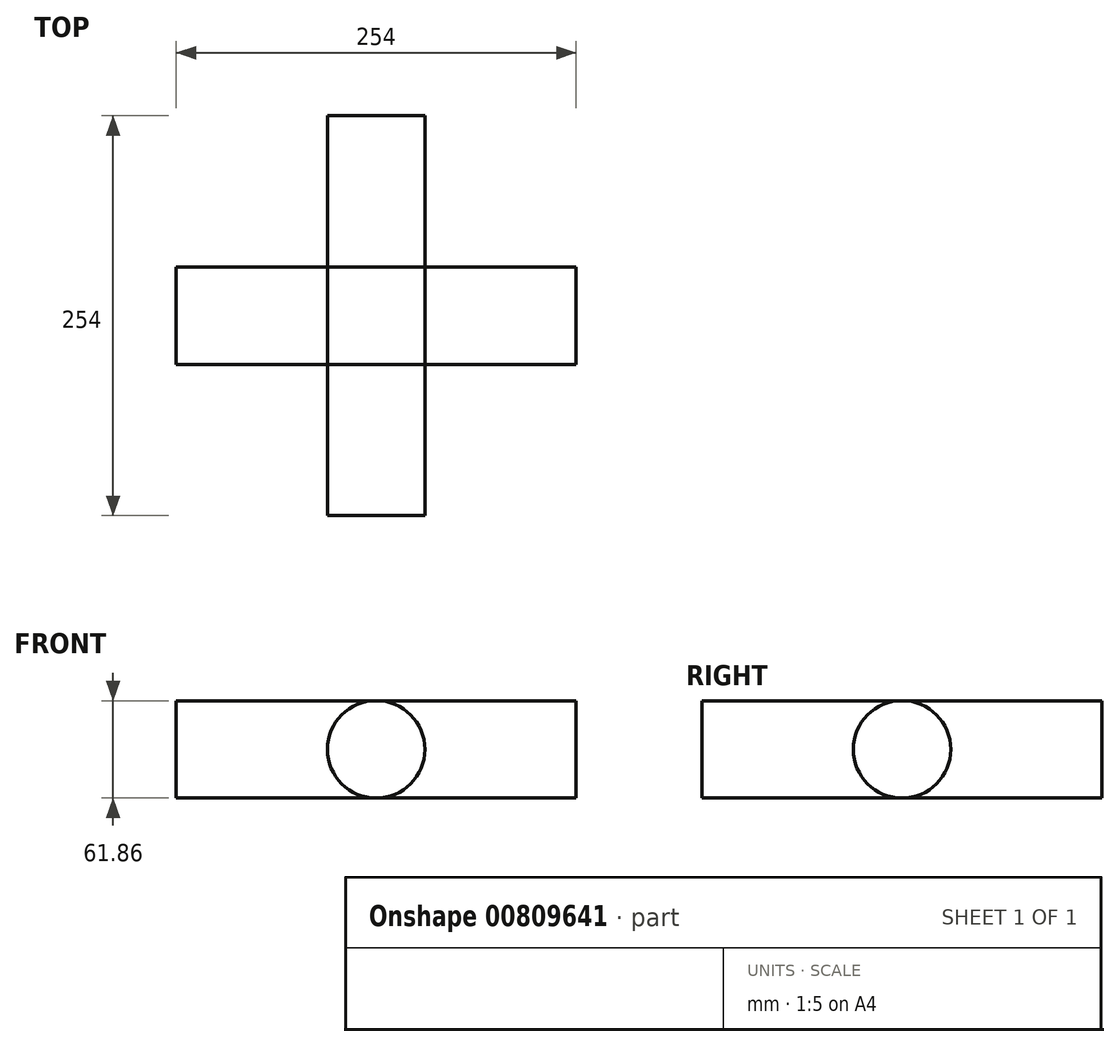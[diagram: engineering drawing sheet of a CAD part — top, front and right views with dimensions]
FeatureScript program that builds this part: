
annotation { "Feature Type Name" : "Feature", "Feature Type Description" : "" }
export const myFeature = defineFeature(function(context is Context, id is Id, definition is map)
    precondition{}
    {
        {
            var Q0;
            Q0=qCreatedBy(makeId("Front.planeOp"),FACE);
            var sketch = newSketch(context, id + "F0", { "sketchPlane" : qUnion([Q0])});
            skCircle(sketch, "E0", {"center": v(0, 0) * mm, "radius": 30.93 * mm});
            skSolve(sketch);
        }
        {
            var Q0;
            Q0 = qSketchRegion(id + "F0", true);
            extrude(context, id + "F1", {"entities" : qUnion([Q0]), "endBound" : BoundingType.SYMMETRIC, "depth" : 254 * mm, "offsetDistance" : 25.4 * mm});
        }
        {
            var Q0;
            Q0=qCreatedBy(makeId("Front.planeOp"),FACE);
            var sketch = newSketch(context, id + "F2", { "sketchPlane" : qUnion([Q0])});
            skLineSegment(sketch, "E1", {"start": v(0, 0) * mm, "end": v(0, 50.23) * mm});
            skSolve(sketch);
        }
        {
            var Q0;
            Q0=makeQuery(id+"F1.opExtrude","SWEPT_BODY",BODY,{"disambiguationData":[OSD([sQuery(id+"F0.wireOp",EDGE,"E0")])]});
            var Q1;
            Q1=sQuery(id+"F2.wireOp",EDGE,"E1");
            circularPattern(context, id + "F3", {"entities" : qUnion([Q0]), "axis" : qUnion([Q1]), "angle" : 360 * degree, "instanceCount" : 4, "equalSpace" : true});
        }
    });
